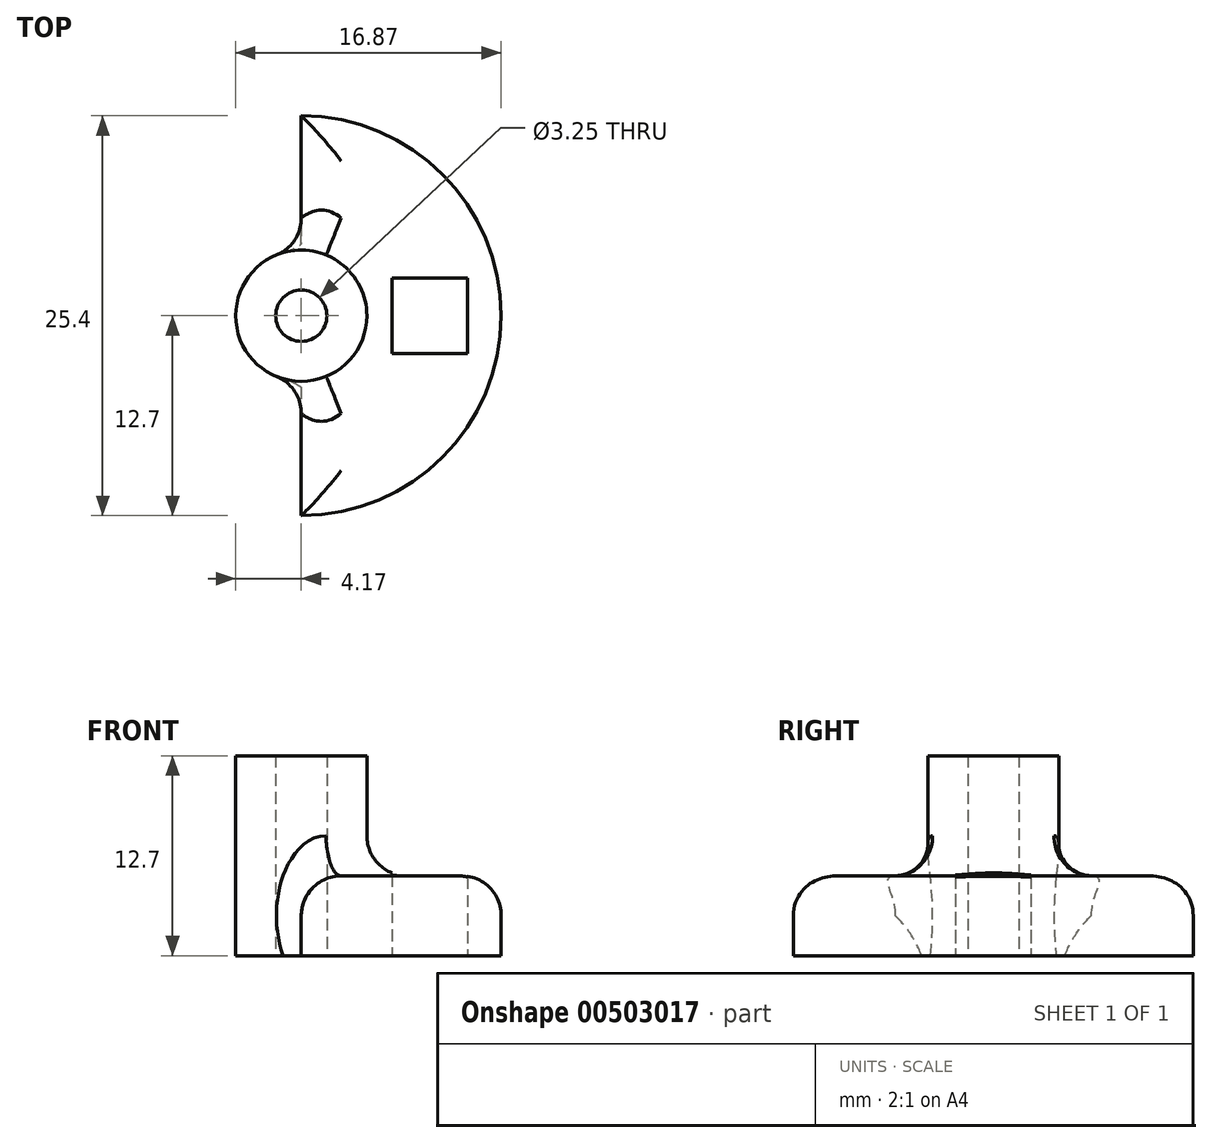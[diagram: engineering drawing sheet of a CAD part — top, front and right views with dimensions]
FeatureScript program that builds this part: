
annotation { "Feature Type Name" : "Feature", "Feature Type Description" : "" }
export const myFeature = defineFeature(function(context is Context, id is Id, definition is map)
    precondition{}
    {
        {
            var Q0;
            Q0=qCreatedBy(makeId("Top.planeOp"),FACE);
            var sketch = newSketch(context, id + "F0", { "sketchPlane" : qUnion([Q0])});
            skCircle(sketch, "E0", {"center": v(0, 0) * mm, "radius": 1.63 * mm});
            skCircle(sketch, "E1", {"center": v(0, 0) * mm, "radius": 4.17 * mm});
            skArc(sketch, "E2", {"start": v(0, -12.7) * mm, "mid": v(12.7, 0) * mm, "end": v(0, 12.7) * mm});
            skLineSegment(sketch, "E3", {"start": v(0, 12.7) * mm, "end": v(0, 4.17) * mm});
            skLineSegment(sketch, "E4", {"start": v(0, -4.17) * mm, "end": v(0, -12.7) * mm});
            skSolve(sketch);
        }
        {
            var Q0;
            Q0=makeQuery(id+"F0.imprint","IMPRINT",FACE,{"disambiguationData":[TD([[makeQuery(id+"F0.imprint","IMPRINT",EDGE,{"derivedFrom":sQuery(id+"F0.wireOp",EDGE,"E0")}),-1.0]])]});
            extrude(context, id + "F1", {"entities" : qUnion([Q0]), "depth" : 12.7 * mm, "offsetDistance" : 25 * mm});
        }
        {
            var Q0;
            Q0=makeQuery(id+"F0.imprint","IMPRINT",FACE,{"disambiguationData":[TD([[makeQuery(id+"F0.imprint","IMPRINT",EDGE,{"derivedFrom":sQuery(id+"F0.wireOp",EDGE,"E2")}),1.0]])]});
            extrude(context, id + "F2", {"entities" : qUnion([Q0]), "operationType" : NewBodyOperationType.ADD, "depth" : 5.08 * mm});
        }
        {
            var Q0;
            Q0=makeQuery(id+"F2.opExtrude","CAP_FACE",FACE,{"disambiguationData":[OSD([sQuery(id+"F0.wireOp",EDGE,"E1"),sQuery(id+"F0.wireOp",EDGE,"E2"),sQuery(id+"F0.wireOp",EDGE,"E3"),sQuery(id+"F0.wireOp",EDGE,"E4")])],"isStart":false});
            fillet(context, id + "F3", {"entities" : qUnion([Q0]), "radius" : 2.54 * mm, "tangentPropagation" : true, "allowEdgeOverflow" : false});
        }
        {
            var Q0;
            Q0=makeQuery(id+"F0.imprint","IMPRINT",FACE,{"disambiguationData":[TD([[makeQuery(id+"F0.imprint","IMPRINT",EDGE,{"derivedFrom":sQuery(id+"F0.wireOp",EDGE,"E2")}),1.0]])]});
            var sketch = newSketch(context, id + "F4", { "sketchPlane" : qUnion([Q0])});
            skLineSegment(sketch, "E5.bottom", {"start": v(10.57, -2.4) * mm, "end": v(5.77, -2.4) * mm});
            skLineSegment(sketch, "E5.top", {"start": v(10.57, 2.4) * mm, "end": v(5.77, 2.4) * mm});
            skLineSegment(sketch, "E5.left", {"start": v(10.57, -2.4) * mm, "end": v(10.57, 2.4) * mm});
            skLineSegment(sketch, "E5.right", {"start": v(5.77, -2.4) * mm, "end": v(5.77, 2.4) * mm});
            skPoint(sketch, "E5.middle", {"position": v(8.17, 0) * mm});
            skSolve(sketch);
        }
        {
            var Q0;
            Q0=makeQuery(id+"F4.imprint","IMPRINT",FACE,{"disambiguationData":[TD([[makeQuery(id+"F4.imprint","IMPRINT",EDGE,{"derivedFrom":sQuery(id+"F4.wireOp",EDGE,"E5.bottom")}),-1.0]])]});
            extrude(context, id + "F5", {"entities" : qUnion([Q0]), "operationType" : NewBodyOperationType.REMOVE, "depth" : 50 * mm, "offsetDistance" : 25 * mm});
        }
    });
